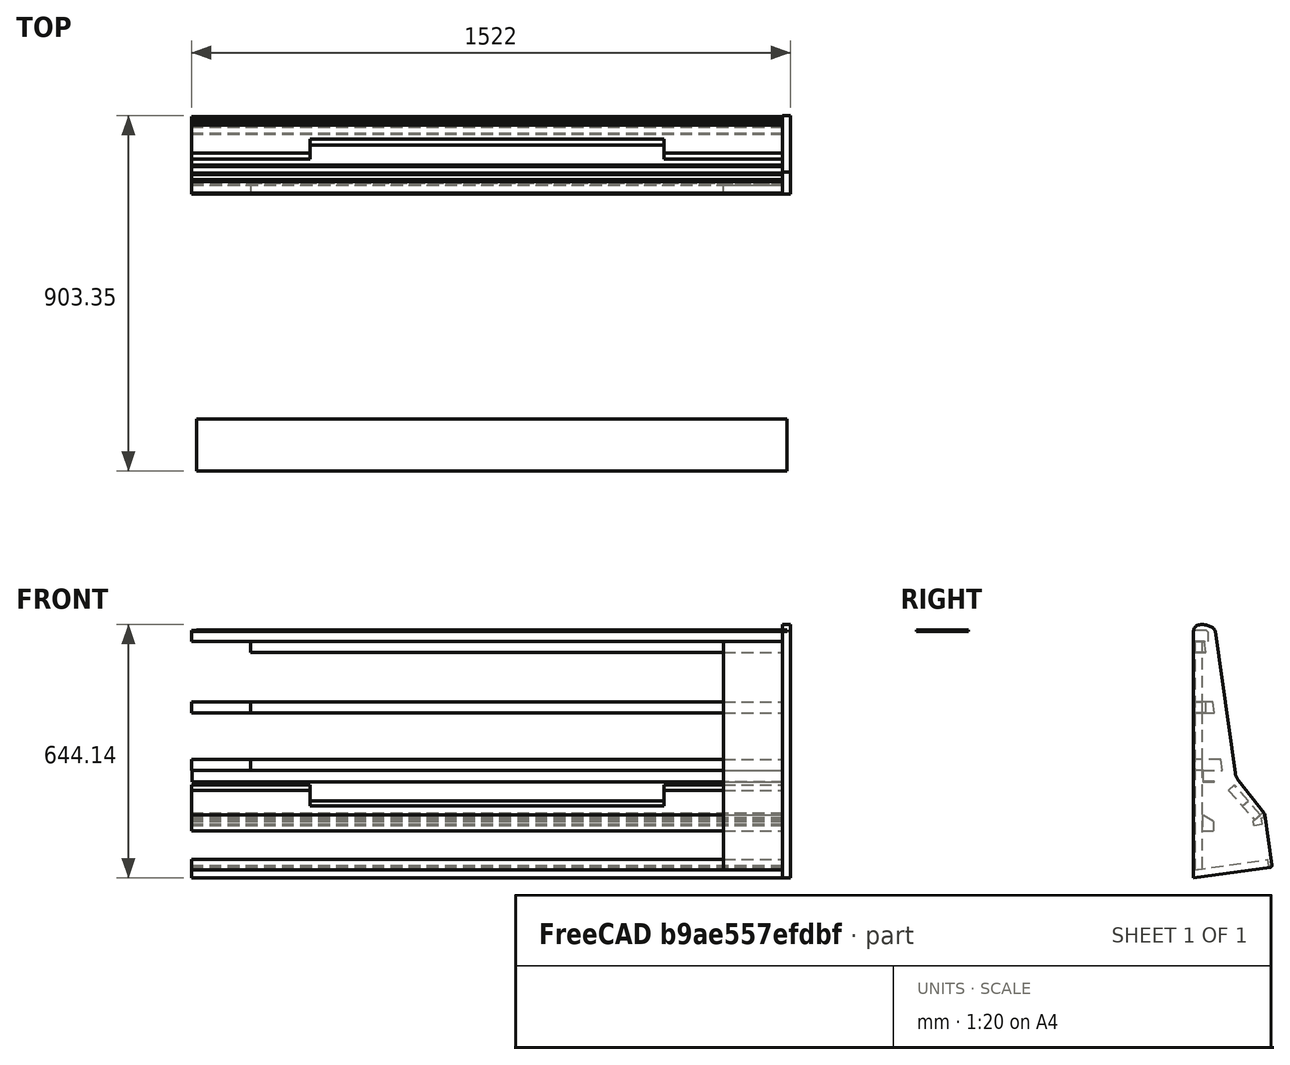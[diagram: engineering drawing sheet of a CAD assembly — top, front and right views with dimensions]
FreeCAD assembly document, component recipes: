
FREECAD ASSEMBLY — COMPONENT RECIPES ("Assemblage_Bati")

This assembly document has 6 components, labeled P0..P5 below (a component is one placed body or linked part). 2 of them carry a construction recipe — the FreeCAD feature program that regenerates the part from scratch, quoted from this document or its linked companion documents; the rest are supplied as boundary geometry only. No exploded tour is included for this assembly.
COMPONENT P0 — geometry summary ("BarreLed"; no construction recipe available for this part):
  bounding box: 1500.0 x 164.7 x 129.2 mm
  tessellated surface: 30,392 triangles
  volume: 8903516 mm^3 (28% of its bounding box)
  symmetry: mirror-symmetric across its x mid-plane
COMPONENT P1 — geometry summary ("BarreSon"; no construction recipe available for this part):
  bounding box: 890.0 x 108.9 x 96.8 mm
  tessellated surface: 6,260 triangles
  volume: 5161515 mm^3 (55% of its bounding box)
  symmetry: mirror-symmetric across its x mid-plane
COMPONENT P2 — recipe-attached ("Armature", modeled in this document).
Construction recipe (the document's own serialized feature program — sketch geometry with constraints, then the solid features built on it; lengths are millimeters unless a unit is written):

FEATURE [Sketcher::SketchObject] Sketch001
  ArcFitTolerance = 1e-06
  AttachmentSupport = -> [YZ_Plane004]
  FullyConstrained = true
  MakeInternals = false
  MapMode = 5
  Placement = pos=(0,0,0) rot=(0.57735,0.57735,0.57735;2.0944rad)
  sketch-geometry (6):
    g0: LineSegment StartX=0 StartY=0 StartZ=0 EndX=36 EndY=0 EndZ=0
    g1: LineSegment StartX=36 StartY=24 StartZ=0 EndX=32 EndY=28 EndZ=0
    g2: LineSegment StartX=32 StartY=28 StartZ=0 EndX=2 EndY=28 EndZ=0
    g3: LineSegment StartX=2 StartY=28 StartZ=0 EndX=0 EndY=26 EndZ=0
    g4: LineSegment StartX=0 StartY=26 StartZ=0 EndX=0 EndY=0 EndZ=0
    g5: LineSegment StartX=36 StartY=24 StartZ=0 EndX=36 EndY=0 EndZ=0
  constraints (17):
    c: Coincident(g-1,g0)
    c: PointOnObject(g0,g-1)
    c: Coincident(g1,g2)
    c: Horizontal(g2)
    c: Coincident(g2,g3)
    c: PointOnObject(g3,g-2)
    c: Coincident(g3,g4)
    c: Coincident(g4,g0)
    c: DistanceX(g0,g0) = 36
    c: Coincident(g5,g1)
    c: Coincident(g5,g0)
    c: Vertical(g5)
    c: DistanceY(g0,g1) = 28
    c: Angle(g1,g5) = 2.35619
    c: Angle(g4,g3) = 2.35619
    c: DistanceX(g2,g2) = 30
    c: DistanceX(g3,g2) = 2
FEATURE [PartDesign::Pad] Pad001
  Direction = (1,0,0)
  Length = 1502
  Length2 = 10
  Placement = pos=(0,0,0) rot=(1,1,1;2.0944rad)
  Profile = -> Sketch001
  ReferenceAxis = -> Sketch001 [N_Axis]
  Refine = true
  Suppressed = false
  Type = 0
FEATURE [PartDesign::Body] Body001  label="Nez"
  AllowCompound = false
  Group = -> [Sketch001,Pad001]
  Origin = -> Origin004
  Placement = pos=(-13.5,704,-26) rot=(0,0,1;0rad)
  Tip = -> Pad001
FEATURE [Sketcher::SketchObject] Sketch004
  ArcFitTolerance = 1e-06
  AttachmentSupport = -> [YZ_Plane006]
  FullyConstrained = true
  MakeInternals = false
  MapMode = 5
  Placement = pos=(0,0,0) rot=(0.57735,0.57735,0.57735;2.0944rad)
  sketch-geometry (4):
    g0: LineSegment StartX=0 StartY=0 StartZ=0 EndX=49.6 EndY=0 EndZ=0
    g1: LineSegment StartX=49.6 StartY=0 StartZ=0 EndX=45.6649 EndY=28 EndZ=0
    g2: LineSegment StartX=45.6649 StartY=28 StartZ=0 EndX=0 EndY=28 EndZ=0
    g3: LineSegment StartX=0 StartY=28 StartZ=0 EndX=0 EndY=0 EndZ=0
  constraints (11):
    c: Coincident(g0,g1)
    c: Coincident(g1,g2)
    c: Coincident(g2,g3)
    c: Coincident(g3,g0)
    c: Horizontal(g0)
    c: Horizontal(g2)
    c: Vertical(g3)
    c: Coincident(g0,g-1)
    c: Angle(g1,g0) = 1.43117
    c: DistanceY(g3,g3) = 28
    c: DistanceX(g0,g0) = 49.6
FEATURE [PartDesign::Pad] Pad003
  Direction = (1,0,0)
  Length = 1502
  Length2 = 10
  Placement = pos=(0,0,0) rot=(1,1,1;2.0944rad)
  Profile = -> Sketch004
  ReferenceAxis = -> Sketch004 [N_Axis]
  Refine = true
  Suppressed = false
  Type = 0
FEATURE [Sketcher::SketchObject] Sketch005
  ArcFitTolerance = 1e-06
  AttachmentSupport = -> [YZ_Plane007]
  FullyConstrained = true
  MakeInternals = false
  MapMode = 5
  Placement = pos=(0,0,0) rot=(0.57735,0.57735,0.57735;2.0944rad)
  sketch-geometry (4):
    g0: LineSegment StartX=0 StartY=0 StartZ=0 EndX=70 EndY=0 EndZ=0
    g1: LineSegment StartX=70 StartY=0 StartZ=0 EndX=66.0649 EndY=28 EndZ=0
    g2: LineSegment StartX=66.0649 StartY=28 StartZ=0 EndX=0 EndY=28 EndZ=0
    g3: LineSegment StartX=0 StartY=28 StartZ=0 EndX=0 EndY=0 EndZ=0
  constraints (11):
    c: Coincident(g0,g1)
    c: Coincident(g1,g2)
    c: Coincident(g2,g3)
    c: Coincident(g3,g0)
    c: Horizontal(g0)
    c: Horizontal(g2)
    c: Vertical(g3)
    c: Coincident(g0,g-1)
    c: Angle(g1,g0) = 1.43117
    c: DistanceY(g3,g3) = 28
    c: DistanceX(g0,g0) = 70
FEATURE [PartDesign::Pad] Pad004
  Direction = (1,0,0)
  Length = 1502
  Length2 = 10
  Placement = pos=(0,0,0) rot=(1,1,1;2.0944rad)
  Profile = -> Sketch005
  ReferenceAxis = -> Sketch005 [N_Axis]
  Refine = true
  Suppressed = false
  Type = 0
FEATURE [Sketcher::SketchObject] Sketch008
  ArcFitTolerance = 1e-06
  AttachmentSupport = -> [YZ_Plane012]
  FullyConstrained = true
  MakeInternals = false
  MapMode = 5
  Placement = pos=(0,0,0) rot=(0.57735,0.57735,0.57735;2.0944rad)
  sketch-geometry (9):
    g0: LineSegment StartX=0 StartY=-20 StartZ=0 EndX=196.879 EndY=-20 EndZ=0
    g1: LineSegment StartX=199 StartY=-17.8787 StartZ=0 EndX=199 EndY=-16 EndZ=0
    g2: LineSegment StartX=192 StartY=0 StartZ=0 EndX=192 EndY=-16 EndZ=0
    g3: LineSegment StartX=192 StartY=-16 StartZ=0 EndX=199 EndY=-16 EndZ=0
    g4: ArcOfCircle [constr] CenterX=196.879 CenterY=-17.8787 CenterZ=0 NormalX=0 NormalY=0 NormalZ=1 AngleXU=0 Radius=2.12132 StartAngle=4.71239 EndAngle=6.28319
    g5: GeomPoint [constr] X=199 Y=-20 Z=0
    g6: LineSegment StartX=196.879 StartY=-20 StartZ=0 EndX=199 EndY=-17.8787 EndZ=0
    g7: LineSegment StartX=0 StartY=-20 StartZ=0 EndX=2.81082 EndY=-1e-16 EndZ=0
    g8: LineSegment StartX=2.81082 StartY=0 StartZ=0 EndX=192 EndY=0 EndZ=0
  constraints (24):
    c: Vertical(g1)
    c: Horizontal(g0)
    c: Vertical(g2)
    c: Coincident(g3,g2)
    c: Horizontal(g3)
    c: PointOnObject(g5,g1)
    c: PointOnObject(g5,g0)
    c: Tangent(g1,g4) = -1.5708
    c: Tangent(g0,g4) = -1.5708
    c: Coincident(g6,g1)
    c: Coincident(g6,g0)
    c: Coincident(g1,g3)
    c: Distance(g6,g6) = 3
    c: Angle(g0,g7) = 1.43117
    c: Coincident(g8,g7)
    c: PointOnObject(g8,g-1)
    c: Horizontal(g8)
    c: Coincident(g2,g8)
    c: Coincident(g0,g7)
    c: Distance(g2,g2) = 16
    c: DistanceY(g0,g-1) = 20
    c: DistanceX(g0,g1) = 199
    c: PointOnObject(g0,g-2)
    c: Distance(g3,g3) = 7
FEATURE [PartDesign::Pad] Pad006
  Direction = (1,0,0)
  Length = 1502
  Length2 = 10
  Placement = pos=(0,0,0) rot=(1,1,1;2.0944rad)
  Profile = -> Sketch008
  ReferenceAxis = -> Sketch008 [N_Axis]
  Refine = true
  Suppressed = false
  Type = 0
FEATURE [PartDesign::Body] Body007  label="Longeron_arriere"
  AllowCompound = false
  Group = -> [Sketch008,Pad006]
  Origin = -> Origin012
  Placement = pos=(-13.5,701.184,-606.82) rot=(-1,0,0;6.14356rad)
  Tip = -> Pad006
FEATURE [Sketcher::SketchObject] Sketch009
  ArcFitTolerance = 1e-06
  AttachmentSupport = -> [YZ_Plane010]
  FullyConstrained = true
  MakeInternals = false
  MapMode = 5
  Placement = pos=(0,0,0) rot=(0.57735,0.57735,0.57735;2.0944rad)
  sketch-geometry (11):
    g0: LineSegment StartX=0 StartY=0 StartZ=0 EndX=21 EndY=0 EndZ=0
    g1: LineSegment StartX=21 StartY=0 StartZ=0 EndX=21 EndY=16 EndZ=0
    g2: LineSegment StartX=21 StartY=16 StartZ=0 EndX=28 EndY=16 EndZ=0
    g3: LineSegment StartX=28 StartY=16 StartZ=0 EndX=28 EndY=23.8066 EndZ=0
    g4: ArcOfCircle [constr] CenterX=23.4098 CenterY=23.8066 CenterZ=0 NormalX=0 NormalY=0 NormalZ=1 AngleXU=0 Radius=4.5902 StartAngle=0 EndAngle=1.15192
    g5: GeomPoint [constr] X=28 Y=28 Z=0
    g6: LineSegment StartX=28 StartY=23.8066 StartZ=0 EndX=25.2768 EndY=28 EndZ=0
    g7: LineSegment StartX=25.2768 StartY=28 StartZ=0 EndX=-1.7e-15 EndY=11.5851 EndZ=0
    g8: LineSegment StartX=0 StartY=0 StartZ=0 EndX=-1.7e-15 EndY=11.5851 EndZ=0
    g9: LineSegment [constr] StartX=25.2768 StartY=28 StartZ=0 EndX=28 EndY=29.7685 EndZ=0
    g10: LineSegment [constr] StartX=28 StartY=29.7685 StartZ=0 EndX=28 EndY=23.8066 EndZ=0
  constraints (29):
    c: Coincident(g0,g-1)
    c: Horizontal(g0)
    c: Coincident(g1,g0)
    c: Vertical(g1)
    c: Coincident(g2,g1)
    c: Horizontal(g2)
    c: Coincident(g3,g2)
    c: Vertical(g3)
    c: Distance(g2,g2) = 7
    c: Distance(g1,g1) = 16
    c: DistanceY(g0,g5) = 28
    c: PointOnObject(g5,g3)
    c: Tangent(g3,g4) = -1.5708
    c: Coincident(g6,g3)
    c: DistanceX(g0,g2) = 28
    c: PointOnObject(g7,g-2)
    c: Coincident(g8,g0)
    c: Coincident(g8,g7)
    c: Angle(g8,g7) = 2.14675
    c: Coincident(g7,g6)
    c: Coincident(g4,g6)
    c: Coincident(g9,g4)
    c: Coincident(g10,g9)
    c: Coincident(g10,g3)
    c: Vertical(g10)
    c: Parallel(g9,g7)
    c: Distance(g6,g6) = 5
    c: Horizontal(g5,g4)
    c: Perpendicular(g7,g6)
FEATURE [PartDesign::Pad] Pad007
  Direction = (1,0,0)
  Length = 1502
  Length2 = 10
  Placement = pos=(0,0,0) rot=(1,1,1;2.0944rad)
  Profile = -> Sketch009
  ReferenceAxis = -> Sketch009 [N_Axis]
  Refine = true
  Suppressed = false
  Type = 0
FEATURE [PartDesign::Body] Body005  label="Longeron_triangle_avant"
  AllowCompound = false
  Group = -> [Sketch009,Pad007]
  Origin = -> Origin010
  Placement = pos=(-13.5,857.737,-492.817) rot=(1,0,0;0.139626rad)
  Tip = -> Pad007
FEATURE [Sketcher::SketchObject] Sketch010
  ArcFitTolerance = 1e-06
  AttachmentSupport = -> [YZ_Plane013]
  FullyConstrained = true
  MakeInternals = false
  MapMode = 5
  Placement = pos=(0,0,0) rot=(0.57735,0.57735,0.57735;2.0944rad)
  sketch-geometry (6):
    g0: LineSegment StartX=0 StartY=0 StartZ=0 EndX=20 EndY=0 EndZ=0
    g1: LineSegment StartX=20 StartY=0 StartZ=0 EndX=20 EndY=100 EndZ=0
    g2: LineSegment [constr] StartX=20 StartY=100 StartZ=0 EndX=0 EndY=100 EndZ=0
    g3: LineSegment [constr] StartX=0 StartY=100 StartZ=0 EndX=0 EndY=0 EndZ=0
    g4: LineSegment StartX=20 StartY=100 StartZ=0 EndX=0 EndY=100 EndZ=0
    g5: LineSegment StartX=0 StartY=100 StartZ=0 EndX=0 EndY=0 EndZ=0
  constraints (16):
    c: Coincident(g0,g1)
    c: Coincident(g1,g2)
    c: Coincident(g2,g3)
    c: Coincident(g3,g0)
    c: Horizontal(g0)
    c: Horizontal(g2)
    c: Vertical(g1)
    c: Vertical(g3)
    c: Distance(g1,g3) = 20
    c: Distance(g0,g2) = 100
    c: Coincident(g0,g-1)
    c: Coincident(g4,g1)
    c: PointOnObject(g4,g3)
    c: Coincident(g5,g4)
    c: Coincident(g5,g0)
    c: Horizontal(g4)
FEATURE [PartDesign::Pad] Pad008
  Direction = (1,0,0)
  Length = 1502
  Length2 = 10
  Placement = pos=(0,0,0) rot=(1,1,1;2.0944rad)
  Profile = -> Sketch010
  ReferenceAxis = -> Sketch010 [N_Axis]
  Refine = true
  Suppressed = false
  Type = 0
FEATURE [Sketcher::SketchObject] Sketch013
  ArcFitTolerance = 1e-06
  AttachmentSupport = -> [YZ_Plane017]
  FullyConstrained = true
  MakeInternals = false
  MapMode = 5
  Placement = pos=(0,0,0) rot=(0.57735,0.57735,0.57735;2.0944rad)
  sketch-geometry (6):
    g0: LineSegment StartX=-3.6e-15 StartY=0 StartZ=0 EndX=28 EndY=0 EndZ=0
    g1: LineSegment [constr] StartX=28 StartY=0 StartZ=0 EndX=28 EndY=40 EndZ=0
    g2: LineSegment [constr] StartX=28 StartY=40 StartZ=0 EndX=-3.6e-15 EndY=40 EndZ=0
    g3: LineSegment StartX=-3.6e-15 StartY=40 StartZ=0 EndX=-3.6e-15 EndY=0 EndZ=0
    g4: LineSegment StartX=28 StartY=23.8342 StartZ=0 EndX=-4.5e-15 EndY=40 EndZ=0
    g5: LineSegment StartX=28 StartY=23.8342 StartZ=0 EndX=28 EndY=0 EndZ=0
  constraints (16):
    c: Coincident(g0,g1)
    c: Coincident(g1,g2)
    c: Coincident(g2,g3)
    c: Coincident(g3,g0)
    c: Horizontal(g0)
    c: Horizontal(g2)
    c: Vertical(g1)
    c: Vertical(g3)
    c: Distance(g1,g3) = 28
    c: Distance(g0,g2) = 40
    c: Coincident(g0,g-1)
    c: PointOnObject(g4,g1)
    c: Coincident(g4,g2)
    c: Angle(g3,g4) = 1.0472
    c: Coincident(g5,g4)
    c: Coincident(g5,g0)
FEATURE [PartDesign::Pad] Pad011
  Direction = (1,0,0)
  Length = 1502
  Length2 = 10
  Placement = pos=(0,0,0) rot=(1,1,1;2.0944rad)
  Profile = -> Sketch013
  ReferenceAxis = -> Sketch013 [N_Axis]
  Refine = true
  Suppressed = false
  Type = 0
FEATURE [PartDesign::Body] Body011  label="Support_barre_son"
  AllowCompound = false
  Group = -> [Sketch013,Pad011]
  Origin = -> Origin017
  Placement = pos=(-13.5,726.949,-506.974) rot=(0,0,1;0rad)
  Tip = -> Pad011
FEATURE [Sketcher::SketchObject] Sketch014
  ArcFitTolerance = 1e-06
  AttachmentSupport = -> [YZ_Plane018]
  FullyConstrained = false
  MakeInternals = false
  MapMode = 5
  Placement = pos=(0,0,0) rot=(0.57735,0.57735,0.57735;2.0944rad)
  sketch-geometry (25):
    g0: LineSegment StartX=0 StartY=0 StartZ=0 EndX=195.049 EndY=27.4123 EndZ=0
    g1: LineSegment StartX=199.304 StartY=33.0596 StartZ=0 EndX=181.481 EndY=159.861 EndZ=0
    g2: LineSegment [constr] StartX=181.108 StartY=162.515 StartZ=0 EndX=107.286 EndY=256.968 EndZ=0
    g3: LineSegment [constr] StartX=107.286 StartY=256.968 StartZ=0 EndX=55.3629 EndY=626.418 EndZ=0
    g4: LineSegment [constr] StartX=52.3921 StartY=629 StartZ=0 EndX=2.12132 EndY=629 EndZ=0
    g5: LineSegment StartX=3.2e-15 StartY=626.879 StartZ=0 EndX=0 EndY=0 EndZ=0
    g6: ArcOfCircle [constr] CenterX=2.12132 CenterY=626.879 CenterZ=0 NormalX=0 NormalY=0 NormalZ=1 AngleXU=0 Radius=2.12132 StartAngle=1.5708 EndAngle=3.14159
    g7: GeomPoint [constr] X=0 Y=629 Z=0
    g8: LineSegment [constr] StartX=2.12132 StartY=629 StartZ=0 EndX=3.1e-15 EndY=626.879 EndZ=0
    g9: ArcOfCircle [constr] CenterX=52.3921 CenterY=626 CenterZ=0 NormalX=0 NormalY=0 NormalZ=1 AngleXU=0 Radius=3 StartAngle=0.139626 EndAngle=1.5708
    g10: GeomPoint [constr] X=55 Y=629 Z=0
    g11-g14: Circle [constr] x4 (B-spline internal-alignment scaffolding for g15; pole/knot coordinates omitted)
    g15: BSplineCurve PolesCount=4 KnotsCount=2 Degree=3 IsPeriodic=0
    g16: GeomPoint [constr] X=3.2e-15 Y=626.879 Z=0
    g17: GeomPoint [constr] X=55.3629 Y=626.418 Z=0
    g18: ArcOfCircle CenterX=145.404 CenterY=273.152 CenterZ=0 NormalX=0 NormalY=0 NormalZ=1 AngleXU=0 Radius=40 StartAngle=3.28122 EndAngle=3.805
    g19: LineSegment StartX=113.888 StartY=248.52 StartZ=0 EndX=179.458 EndY=164.627 EndZ=0
    g20: LineSegment StartX=105.793 StartY=267.586 StartZ=0 EndX=55.3629 EndY=626.418 EndZ=0
    g21: ArcOfCircle CenterX=171.579 CenterY=158.469 CenterZ=0 NormalX=0 NormalY=0 NormalZ=1 AngleXU=0 Radius=10 StartAngle=0.139642 EndAngle=0.663406
    g22: GeomPoint [constr] X=181.108 Y=162.515 Z=0
    g23: ArcOfCircle CenterX=194.353 CenterY=32.3636 CenterZ=0 NormalX=0 NormalY=0 NormalZ=1 AngleXU=0 Radius=5 StartAngle=4.85202 EndAngle=6.42283
    g24: GeomPoint [constr] X=200 Y=28.1082 Z=0
  constraints (49):
    c: Coincident(g0,g-1)
    c: Coincident(g2,g22)
    c: Coincident(g3,g2)
    c: PointOnObject(g7,g-2)
    c: Horizontal(g4)
    c: Coincident(g5,g0)
    c: Angle(g0,g5) = 1.43117
    c: DistanceX(g0,g24) = 200
    c: DistanceX(g7,g10) = 55
    c: DistanceY(g5,g7) = 629
    c: PointOnObject(g7,g4)
    c: PointOnObject(g7,g5)
    c: Tangent(g4,g6) = -1.5708
    c: Tangent(g5,g6) = -1.5708
    c: Coincident(g8,g4)
    c: Coincident(g8,g5)
    c: Distance(g8,g8) = 3
    c: PointOnObject(g10,g4)
    c: PointOnObject(g10,g3)
    c: Tangent(g4,g9) = -1.5708
    c: Tangent(g3,g9) = -1.5708
    c: Angle(g4,g3) = 1.71042
    c: Radius(g9) = 3
    c: Weight(g11) = 1
    c: Equal(g11,g12)
    c: Equal(g11,g13)
    c: Equal(g11,g14)
    c: InternalAlignment(g11-g14 -> g15) x4
    c: InternalAlignment(g16,g15)
    c: InternalAlignment(g17,g15)
    c: Coincident(g11,g5)
    c: Coincident(g14,g3)
    c: Vertical(g12,g15)
    c: Tangent(g18,g2) = 1.5708
    c: Tangent(g18,g3) = 1.5708
    c: Diameter(g18) = 80
    c: Coincident(g19,g18)
    c: Coincident(g20,g18)
    c: Coincident(g20,g15)
    c: PointOnObject(g22,g1)
    c: PointOnObject(g22,g19)
    c: Tangent(g1,g21) = -1.5708
    c: Tangent(g19,g21) = 1.5708
    c: Radius(g21) = 10
    c: PointOnObject(g24,g0)
    c: PointOnObject(g24,g1)
    c: Tangent(g0,g23) = -1.5708
    c: Tangent(g1,g23) = -1.5708
    c: Radius(g23) = 5
FEATURE [PartDesign::Pad] Pad012
  Direction = (1,0,0)
  Length = 20
  Length2 = 10
  Placement = pos=(0,0,0) rot=(1,1,1;2.0944rad)
  Profile = -> Sketch014
  ReferenceAxis = -> Sketch014 [N_Axis]
  Refine = true
  Suppressed = false
  Type = 0
FEATURE [PartDesign::Body] Body012  label="Flanc"
  AllowCompound = false
  Group = -> [Sketch014,Pad012]
  Origin = -> Origin018
  Placement = pos=(-33.4,704,-627) rot=(0,0,1;0rad)
  Tip = -> Pad012
FEATURE [Sketcher::SketchObject] Sketch015
  ArcFitTolerance = 1e-06
  AttachmentSupport = -> [YZ_Plane019]
  FullyConstrained = true
  MakeInternals = false
  MapMode = 5
  Placement = pos=(0,0,0) rot=(0.57735,0.57735,0.57735;2.0944rad)
  sketch-geometry (6):
    g0: LineSegment StartX=0 StartY=0 StartZ=0 EndX=30 EndY=0 EndZ=0
    g1: LineSegment StartX=30 StartY=0 StartZ=0 EndX=30 EndY=1.5 EndZ=0
    g2: LineSegment StartX=30 StartY=1.5 StartZ=0 EndX=1.5 EndY=1.5 EndZ=0
    g3: LineSegment StartX=1.5 StartY=1.5 StartZ=0 EndX=1.5 EndY=30 EndZ=0
    g4: LineSegment StartX=1.5 StartY=30 StartZ=0 EndX=0 EndY=30 EndZ=0
    g5: LineSegment StartX=0 StartY=30 StartZ=0 EndX=0 EndY=0 EndZ=0
  constraints (17):
    c: Distance(g0) = 30
    c: Coincident(g0,g-1)
    c: PointOnObject(g0,g-1)
    c: Distance(g1) = 1.5
    c: Coincident(g1,g0)
    c: Vertical(g1)
    c: Coincident(g2,g1)
    c: Horizontal(g2)
    c: Coincident(g3,g2)
    c: Vertical(g3)
    c: Coincident(g4,g3)
    c: PointOnObject(g4,g-2)
    c: Horizontal(g4)
    c: Coincident(g5,g4)
    c: Coincident(g5,g0)
    c: Equal(g4,g1)
    c: Equal(g0,g5)
FEATURE [PartDesign::Pad] Pad013
  Direction = (1,0,0)
  Length = 1500
  Length2 = 10
  Placement = pos=(0,0,0) rot=(1,1,1;2.0944rad)
  Profile = -> Sketch015
  ReferenceAxis = -> Sketch015 [N_Axis]
  Refine = true
  Suppressed = false
  Type = 0
FEATURE [PartDesign::Body] Body013  label="Corniere_aluminium"
  AllowCompound = false
  Group = -> [Sketch015,Pad013]
  Origin = -> Origin019
  Placement = pos=(-12,727.1,-383) rot=(0,0,1;0rad)
  Tip = -> Pad013
FEATURE [Sketcher::SketchObject] Sketch016
  ArcFitTolerance = 1e-06
  AttachmentSupport = -> [Pad003]
  FullyConstrained = true
  MakeInternals = false
  MapMode = 5
  Placement = pos=(0,0,0) rot=(0.707107,0.707107,0;3.14159rad)
  sketch-geometry (8):
    g0: LineSegment StartX=0 StartY=0 StartZ=0 EndX=28 EndY=0 EndZ=0
    g1: LineSegment StartX=28 StartY=0 StartZ=0 EndX=28 EndY=150 EndZ=0
    g2: LineSegment StartX=28 StartY=150 StartZ=0 EndX=0 EndY=150 EndZ=0
    g3: LineSegment StartX=0 StartY=150 StartZ=0 EndX=0 EndY=0 EndZ=0
    g4: LineSegment StartX=0 StartY=1502 StartZ=0 EndX=0 EndY=1352 EndZ=0
    g5: LineSegment StartX=0 StartY=1352 StartZ=0 EndX=20 EndY=1352 EndZ=0
    g6: LineSegment StartX=20 StartY=1352 StartZ=0 EndX=20 EndY=1502 EndZ=0
    g7: LineSegment StartX=20 StartY=1502 StartZ=0 EndX=0 EndY=1502 EndZ=0
  constraints (23):
    c: Coincident(g0,g1)
    c: Coincident(g1,g2)
    c: Coincident(g2,g3)
    c: Coincident(g3,g0)
    c: Horizontal(g0)
    c: Horizontal(g2)
    c: Vertical(g1)
    c: Vertical(g3)
    c: Coincident(g0,g-1)
    c: DistanceY(g3,g3) = 150
    c: Distance(g2,g2) = 28
    c: Coincident(g4,g5)
    c: Coincident(g5,g6)
    c: Coincident(g6,g7)
    c: Coincident(g7,g4)
    c: Vertical(g4)
    c: Vertical(g6)
    c: Horizontal(g5)
    c: Horizontal(g7)
    c: DistanceY(g4,g4) = 150
    c: Distance(g7,g7) = 20
    c: PointOnObject(g4,g-2)
    c: DistanceY(g0,g4) = 1502
FEATURE [PartDesign::Pocket] Pocket
  BaseFeature = -> Pad003
  Direction = (0,0,1)
  Length = 5
  Length2 = 5
  Placement = pos=(0,0,0) rot=(1,1,1;2.0944rad)
  Profile = -> Sketch016
  ReferenceAxis = -> Sketch016 [N_Axis]
  Refine = true
  Suppressed = false
  Type = 1
FEATURE [PartDesign::Body] Body003  label="Longeron_central_tableJeu"
  AllowCompound = false
  Group = -> [Sketch004,Pad003,Sketch016,Pocket]
  Origin = -> Origin006
  Placement = pos=(-13.5,707,-207.5) rot=(0,0,1;0rad)
  Tip = -> Pocket
FEATURE [Sketcher::SketchObject] Sketch017
  ArcFitTolerance = 1e-06
  AttachmentSupport = -> [Pad004]
  FullyConstrained = true
  MakeInternals = false
  MapMode = 5
  Placement = pos=(0,0,0) rot=(0.707107,0.707107,0;3.14159rad)
  sketch-geometry (8):
    g0: LineSegment StartX=0 StartY=0 StartZ=0 EndX=20 EndY=0 EndZ=0
    g1: LineSegment StartX=20 StartY=0 StartZ=0 EndX=20 EndY=150 EndZ=0
    g2: LineSegment StartX=20 StartY=150 StartZ=0 EndX=0 EndY=150 EndZ=0
    g3: LineSegment StartX=0 StartY=150 StartZ=0 EndX=0 EndY=0 EndZ=0
    g4: LineSegment StartX=0 StartY=1352 StartZ=0 EndX=20 EndY=1352 EndZ=0
    g5: LineSegment StartX=20 StartY=1352 StartZ=0 EndX=20 EndY=1502 EndZ=0
    g6: LineSegment StartX=20 StartY=1502 StartZ=0 EndX=0 EndY=1502 EndZ=0
    g7: LineSegment StartX=0 StartY=1502 StartZ=0 EndX=0 EndY=1352 EndZ=0
  constraints (23):
    c: Coincident(g0,g1)
    c: Coincident(g1,g2)
    c: Coincident(g2,g3)
    c: Coincident(g3,g0)
    c: Horizontal(g0)
    c: Horizontal(g2)
    c: Vertical(g1)
    c: Vertical(g3)
    c: Distance(g0,g0) = 20
    c: DistanceY(g3,g3) = 150
    c: Coincident(g4,g5)
    c: Coincident(g5,g6)
    c: Coincident(g6,g7)
    c: Coincident(g7,g4)
    c: Horizontal(g4)
    c: Horizontal(g6)
    c: Vertical(g5)
    c: Vertical(g7)
    c: Equal(g7,g3)
    c: Equal(g4,g2)
    c: DistanceY(g0,g6) = 1502
    c: Coincident(g0,g-1)
    c: PointOnObject(g6,g-2)
FEATURE [PartDesign::Pocket] Pocket001
  BaseFeature = -> Pad004
  Direction = (0,0,1)
  Length = 5
  Length2 = 5
  Placement = pos=(0,0,0) rot=(1,1,1;2.0944rad)
  Profile = -> Sketch017
  ReferenceAxis = -> Sketch017 [N_Axis]
  Refine = true
  Suppressed = false
  Type = 1
FEATURE [PartDesign::Body] Body004  label="Longeron_arriere_tableJeu"
  AllowCompound = false
  Group = -> [Sketch005,Pad004,Sketch017,Pocket001]
  Origin = -> Origin007
  Placement = pos=(-13.5,707,-353) rot=(0,0,1;0rad)
  Tip = -> Pocket001
FEATURE [Sketcher::SketchObject] Sketch018
  ArcFitTolerance = 1e-06
  AttachmentSupport = -> [YZ_Plane003]
  FullyConstrained = true
  MakeInternals = false
  MapMode = 5
  Placement = pos=(0,0,0) rot=(0.57735,0.57735,0.57735;2.0944rad)
  sketch-geometry (6):
    g0: LineSegment [constr] StartX=0 StartY=0 StartZ=0 EndX=20 EndY=0 EndZ=0
    g1: LineSegment [constr] StartX=20 StartY=0 StartZ=0 EndX=20 EndY=580 EndZ=0
    g2: LineSegment StartX=20 StartY=580 StartZ=0 EndX=0 EndY=580 EndZ=0
    g3: LineSegment StartX=0 StartY=580 StartZ=0 EndX=0 EndY=0 EndZ=0
    g4: LineSegment StartX=0 StartY=0 StartZ=0 EndX=20 EndY=2.81082 EndZ=0
    g5: LineSegment StartX=20 StartY=2.81082 StartZ=0 EndX=20 EndY=580 EndZ=0
  constraints (16):
    c: Coincident(g0,g1)
    c: Coincident(g1,g2)
    c: Coincident(g2,g3)
    c: Coincident(g3,g0)
    c: Horizontal(g0)
    c: Horizontal(g2)
    c: Vertical(g1)
    c: Vertical(g3)
    c: Coincident(g4,g0)
    c: PointOnObject(g4,g1)
    c: Coincident(g5,g4)
    c: Coincident(g5,g1)
    c: Distance(g2,g2) = 20
    c: Angle(g4,g3) = 1.43117
    c: Coincident(g0,g-1)
    c: DistanceY(g3,g3) = 580
FEATURE [PartDesign::Pad] Pad014
  Direction = (1,0,0)
  Length = 150
  Length2 = 10
  Placement = pos=(0,0,0) rot=(1,1,1;2.0944rad)
  Profile = -> Sketch018
  ReferenceAxis = -> Sketch018 [N_Axis]
  Refine = true
  Suppressed = false
  Type = 0
FEATURE [PartDesign::Body] Body  label="Longeron_fixation_pied"
  AllowCompound = false
  Group = -> [Sketch018,Pad014]
  Origin = -> Origin003
  Placement = pos=(-13.5,707,-606) rot=(0,0,1;0rad)
  Tip = -> Pad014
FEATURE [PartDesign::FeatureBase] Clone
  BaseFeature = -> Body
  Placement = pos=(-12.5,707,-606) rot=(0,0,1;0rad)
  Suppressed = false
FEATURE [PartDesign::Body] Body014  label="Longeron_fixation_pied_2"
  AllowCompound = false
  Group = -> [Clone]
  Origin = -> Origin020
  Placement = pos=(1351,0,0) rot=(0,0,1;0rad)
  Tip = -> Clone
FEATURE [PartDesign::FeatureBase] Clone001
  BaseFeature = -> Body012
  Placement = pos=(-40.5,704,-634.8) rot=(0,0,1;0rad)
  Suppressed = false
FEATURE [PartDesign::Body] Body015  label="Flanc_2"
  AllowCompound = false
  Group = -> [Clone001]
  Origin = -> Origin021
  Placement = pos=(1529,0,7.8) rot=(0,0,1;0rad)
  Tip = -> Clone001
FEATURE [Sketcher::SketchObject] Sketch
  ArcFitTolerance = 1e-06
  AttachmentSupport = -> [XZ_Plane013]
  FullyConstrained = true
  MakeInternals = false
  MapMode = 5
  Placement = pos=(0,0,0) rot=(1,0,0;1.5708rad)
  sketch-geometry (4):
    g0: LineSegment StartX=301 StartY=147 StartZ=0 EndX=301 EndY=47 EndZ=0
    g1: LineSegment StartX=301 StartY=47 StartZ=0 EndX=1201 EndY=47 EndZ=0
    g2: LineSegment StartX=1201 StartY=47 StartZ=0 EndX=1201 EndY=147 EndZ=0
    g3: LineSegment StartX=1201 StartY=147 StartZ=0 EndX=301 EndY=147 EndZ=0
  constraints (12):
    c: Coincident(g0,g1)
    c: Coincident(g1,g2)
    c: Coincident(g2,g3)
    c: Coincident(g3,g0)
    c: Vertical(g0)
    c: Vertical(g2)
    c: Horizontal(g1)
    c: Horizontal(g3)
    c: DistanceX(g3,g3) = 900
    c: Distance(g-2,g0) = 301
    c: DistanceY(g-1,g0) = 47
    c: DistanceY(g0,g0) = 100
FEATURE [PartDesign::Pocket] Pocket002
  BaseFeature = -> Pad008
  Direction = (0,1,-2e-16)
  Length = 5
  Length2 = 5
  Placement = pos=(0,0,0) rot=(1,1,1;2.0944rad)
  Profile = -> Sketch
  ReferenceAxis = -> Sketch [N_Axis]
  Refine = true
  Suppressed = false
  Type = 1
FEATURE [PartDesign::Body] Body008  label="Longeron_cartel"
  AllowCompound = false
  Group = -> [Sketch010,Pad008,Sketch,Pocket002]
  Origin = -> Origin013
  Placement = pos=(-13.5,858.569,-479.357) rot=(1,0,0;0.715585rad)
  Tip = -> Pocket002
FEATURE [Sketcher::SketchObject] Sketch019
  ArcFitTolerance = 1e-06
  AttachmentSupport = -> [YZ_Plane022]
  FullyConstrained = true
  MakeInternals = false
  MapMode = 5
  Placement = pos=(0,0,0) rot=(0.57735,0.57735,0.57735;2.0944rad)
  sketch-geometry (4):
    g0: LineSegment StartX=0 StartY=0 StartZ=0 EndX=28 EndY=0 EndZ=0
    g1: LineSegment StartX=28 StartY=0 StartZ=0 EndX=24.0649 EndY=28 EndZ=0
    g2: LineSegment StartX=24.0649 StartY=28 StartZ=0 EndX=0 EndY=28 EndZ=0
    g3: LineSegment StartX=0 StartY=28 StartZ=0 EndX=0 EndY=0 EndZ=0
  constraints (11):
    c: Coincident(g0,g1)
    c: Coincident(g1,g2)
    c: Coincident(g2,g3)
    c: Coincident(g3,g0)
    c: Horizontal(g0)
    c: Horizontal(g2)
    c: Vertical(g3)
    c: Coincident(g0,g-1)
    c: Angle(g1,g0) = 1.43117
    c: DistanceY(g3,g3) = 28
    c: DistanceX(g0,g0) = 28
FEATURE [PartDesign::Pad] Pad015
  Direction = (1,0,0)
  Length = 1502
  Length2 = 10
  Placement = pos=(0,0,0) rot=(1,1,1;2.0944rad)
  Profile = -> Sketch019
  ReferenceAxis = -> Sketch019 [N_Axis]
  Refine = true
  Suppressed = false
  Type = 0
FEATURE [Sketcher::SketchObject] Sketch020
  ArcFitTolerance = 1e-06
  AttachmentSupport = -> [Pad015]
  FullyConstrained = true
  MakeInternals = false
  MapMode = 5
  Placement = pos=(0,0,0) rot=(0.707107,0.707107,0;3.14159rad)
  sketch-geometry (8):
    g0: LineSegment StartX=0 StartY=0 StartZ=0 EndX=28 EndY=0 EndZ=0
    g1: LineSegment StartX=28 StartY=0 StartZ=0 EndX=28 EndY=150 EndZ=0
    g2: LineSegment StartX=28 StartY=150 StartZ=0 EndX=0 EndY=150 EndZ=0
    g3: LineSegment StartX=0 StartY=150 StartZ=0 EndX=0 EndY=0 EndZ=0
    g4: LineSegment StartX=0 StartY=1502 StartZ=0 EndX=0 EndY=1352 EndZ=0
    g5: LineSegment StartX=0 StartY=1352 StartZ=0 EndX=20 EndY=1352 EndZ=0
    g6: LineSegment StartX=20 StartY=1352 StartZ=0 EndX=20 EndY=1502 EndZ=0
    g7: LineSegment StartX=20 StartY=1502 StartZ=0 EndX=0 EndY=1502 EndZ=0
  constraints (23):
    c: Coincident(g0,g1)
    c: Coincident(g1,g2)
    c: Coincident(g2,g3)
    c: Coincident(g3,g0)
    c: Horizontal(g0)
    c: Horizontal(g2)
    c: Vertical(g1)
    c: Vertical(g3)
    c: Coincident(g0,g-1)
    c: DistanceY(g3,g3) = 150
    c: Distance(g2,g2) = 28
    c: Coincident(g4,g5)
    c: Coincident(g5,g6)
    c: Coincident(g6,g7)
    c: Coincident(g7,g4)
    c: Vertical(g4)
    c: Vertical(g6)
    c: Horizontal(g5)
    c: Horizontal(g7)
    c: DistanceY(g4,g4) = 150
    c: Distance(g7,g7) = 20
    c: PointOnObject(g4,g-2)
    c: DistanceY(g0,g4) = 1502
FEATURE [PartDesign::Pocket] Pocket003
  BaseFeature = -> Pad015
  Direction = (0,0,1)
  Length = 5
  Length2 = 5
  Placement = pos=(0,0,0) rot=(1,1,1;2.0944rad)
  Profile = -> Sketch020
  ReferenceAxis = -> Sketch020 [N_Axis]
  Refine = true
  Suppressed = false
  Type = 1
FEATURE [PartDesign::Body] Body016  label="Longeron_frontal"
  AllowCompound = false
  Group = -> [Sketch019,Pad015,Sketch020,Pocket003]
  Origin = -> Origin022
  Placement = pos=(-13.5,707,-54) rot=(0,0,1;0rad)
  Tip = -> Pocket003
COMPONENT P3 — recipe-attached ("Cartel_barre_son", modeled in this document).
Construction recipe (the document's own serialized feature program — sketch geometry with constraints, then the solid features built on it; lengths are millimeters unless a unit is written):

FEATURE [Sketcher::SketchObject] Sketch011
  ArcFitTolerance = 1e-06
  AttachmentSupport = -> [YZ_Plane015]
  FullyConstrained = true
  MakeInternals = false
  MapMode = 5
  Placement = pos=(0,0,0) rot=(0.57735,0.57735,0.57735;2.0944rad)
  sketch-geometry (4):
    g0: LineSegment StartX=0 StartY=0 StartZ=0 EndX=132 EndY=0 EndZ=0
    g1: LineSegment StartX=132 StartY=0 StartZ=0 EndX=132 EndY=3 EndZ=0
    g2: LineSegment StartX=132 StartY=3 StartZ=0 EndX=0 EndY=3 EndZ=0
    g3: LineSegment StartX=0 StartY=3 StartZ=0 EndX=0 EndY=0 EndZ=0
  constraints (11):
    c: Coincident(g0,g1)
    c: Coincident(g1,g2)
    c: Coincident(g2,g3)
    c: Coincident(g3,g0)
    c: Horizontal(g0)
    c: Horizontal(g2)
    c: Vertical(g1)
    c: Vertical(g3)
    c: Coincident(g0,g-1)
    c: Distance(g1,g1) = 3
    c: DistanceX(g2,g2) = 132
FEATURE [PartDesign::Pad] Pad009
  Direction = (1,0,0)
  Length = 1500
  Length2 = 10
  Placement = pos=(0,0,0) rot=(1,1,1;2.0944rad)
  Profile = -> Sketch011
  ReferenceAxis = -> Sketch011 [N_Axis]
  Refine = true
  Suppressed = false
  Type = 0
FEATURE [PartDesign::Body] Body009  label="Cartel"
  AllowCompound = false
  Group = -> [Sketch011,Pad009]
  Origin = -> Origin015
  Tip = -> Pad009
COMPONENT P4 — geometry summary ("Pieds"; no construction recipe available for this part):
  bounding box: 1497.0 x 712.0 x 580.0 mm
  tessellated surface: 2,072 triangles
  volume: 19063206 mm^3 (3% of its bounding box)
  symmetry: 2-fold rotationally symmetric about the z axis; mirror-symmetric across its x mid-plane, y mid-plane
COMPONENT P5 — geometry summary ("TableJeu"; no construction recipe available for this part):
  bounding box: 361.4 x 150.0 x 67.5 mm
  tessellated surface: 4,364 triangles
  volume: 320182 mm^3 (9% of its bounding box)
  symmetry: mirror-symmetric across its x mid-plane
PROVENANCE & LICENSES
A FreeCAD (.FCStd) document from a public repository crawl; recipes are the document's own serialized feature recipes (and, for linked parts, companion documents' recipes).
License: cern-ohl.
